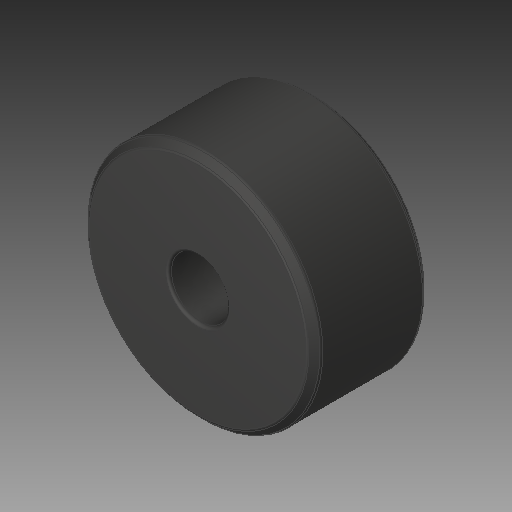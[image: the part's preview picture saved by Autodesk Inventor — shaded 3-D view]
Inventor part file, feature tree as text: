
AUTODESK INVENTOR PART (.ipt)
format: ipt  version: 2019 (Build 230136000, 136)  size: 142,336 bytes
history: mixed  units: mm
features: other x1, fillet x1, imported_body x1
ambient origin geometry x8: Origin, YZ Plane, XZ Plane, XY Plane, X Axis, Y Axis, Z Axis, Center Point
bodies: Body1 (imported_parasolid)
feature tree (3):
  other  "Твердое тело1"
  fillet  "Fillet1"  [1 undecoded]
  imported_body  NMx_Import_Brep_tag  [imported B-rep: ~12 faces, bbox_mm=[8.0, 0.0, 4.0]]
note: 1 required parameter value undecoded (feature->parameter linkage not recoverable at this tier; creation-order binding heuristic only, values carry confidence <= 0.55)
